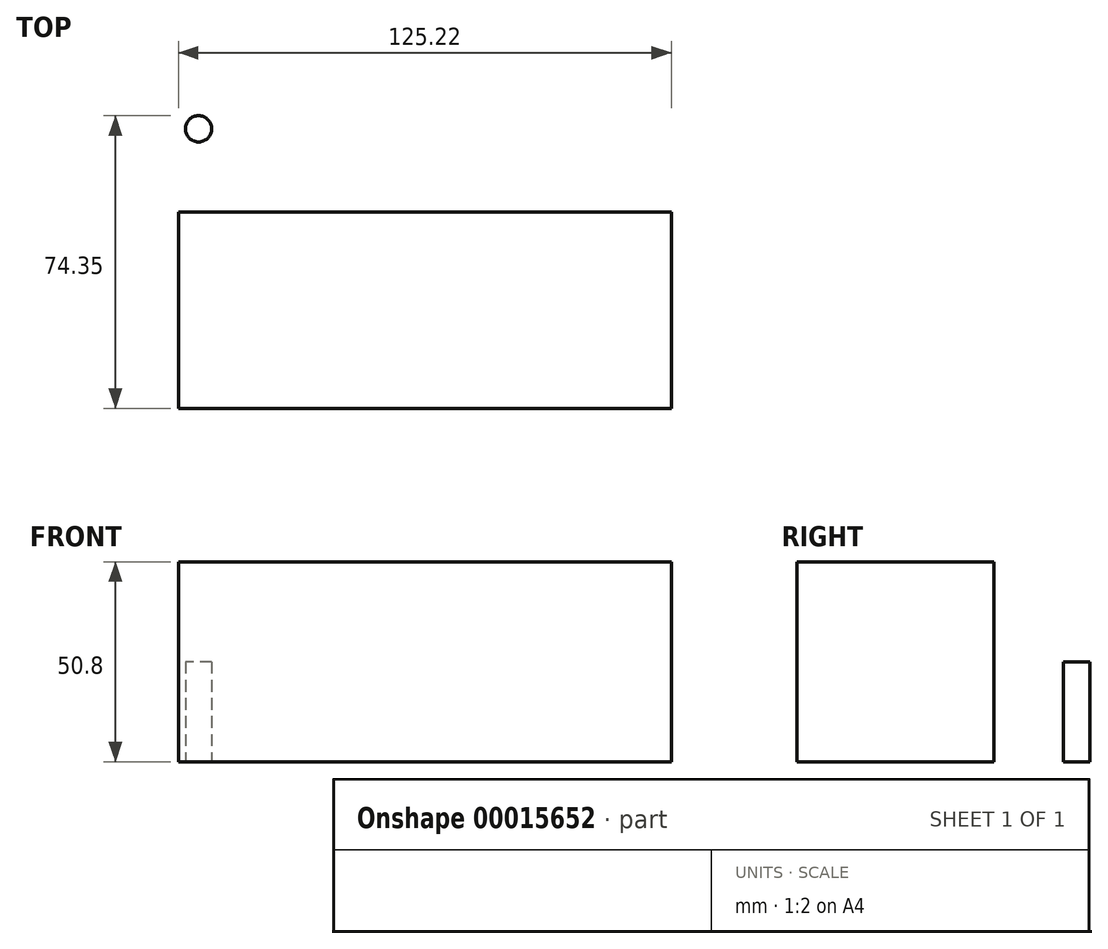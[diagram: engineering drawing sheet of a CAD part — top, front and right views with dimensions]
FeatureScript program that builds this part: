
annotation { "Feature Type Name" : "Feature", "Feature Type Description" : "" }
export const myFeature = defineFeature(function(context is Context, id is Id, definition is map)
    precondition{}
    {
        {
            var Q0;
            Q0=qCreatedBy(makeId("Top.planeOp"),FACE);
            var sketch = newSketch(context, id + "F0", { "sketchPlane" : qUnion([Q0])});
            skCircle(sketch, "E0", {"center": v(-57.33, 34.94) * mm, "radius": 3.33 * mm});
            skSolve(sketch);
        }
        {
            var Q0;
            Q0=makeQuery(id+"F0.imprint","IMPRINT",FACE,{"disambiguationData":[TD([[makeQuery(id+"F0.imprint","IMPRINT",EDGE,{"derivedFrom":sQuery(id+"F0.wireOp",EDGE,"E0")}),1.0]])]});
            extrude(context, id + "F1", {"entities" : qUnion([Q0]), "depth" : 25.4 * mm});
        }
        {
            var Q0;
            Q0=qCreatedBy(makeId("Top.planeOp"),FACE);
            var sketch = newSketch(context, id + "F2", { "sketchPlane" : qUnion([Q0])});
            skLineSegment(sketch, "E1.bottom", {"start": v(-62.47, 13.83) * mm, "end": v(62.75, 13.83) * mm});
            skLineSegment(sketch, "E1.top", {"start": v(-62.47, -36.08) * mm, "end": v(62.75, -36.08) * mm});
            skLineSegment(sketch, "E1.left", {"start": v(-62.47, 13.83) * mm, "end": v(-62.47, -36.08) * mm});
            skLineSegment(sketch, "E1.right", {"start": v(62.75, 13.83) * mm, "end": v(62.75, -36.08) * mm});
            skSolve(sketch);
        }
        {
            var Q0;
            Q0 = qSketchRegion(id + "F2", true);
            extrude(context, id + "F3", {"entities" : qUnion([Q0]), "depth" : 50.8 * mm});
        }
    });
